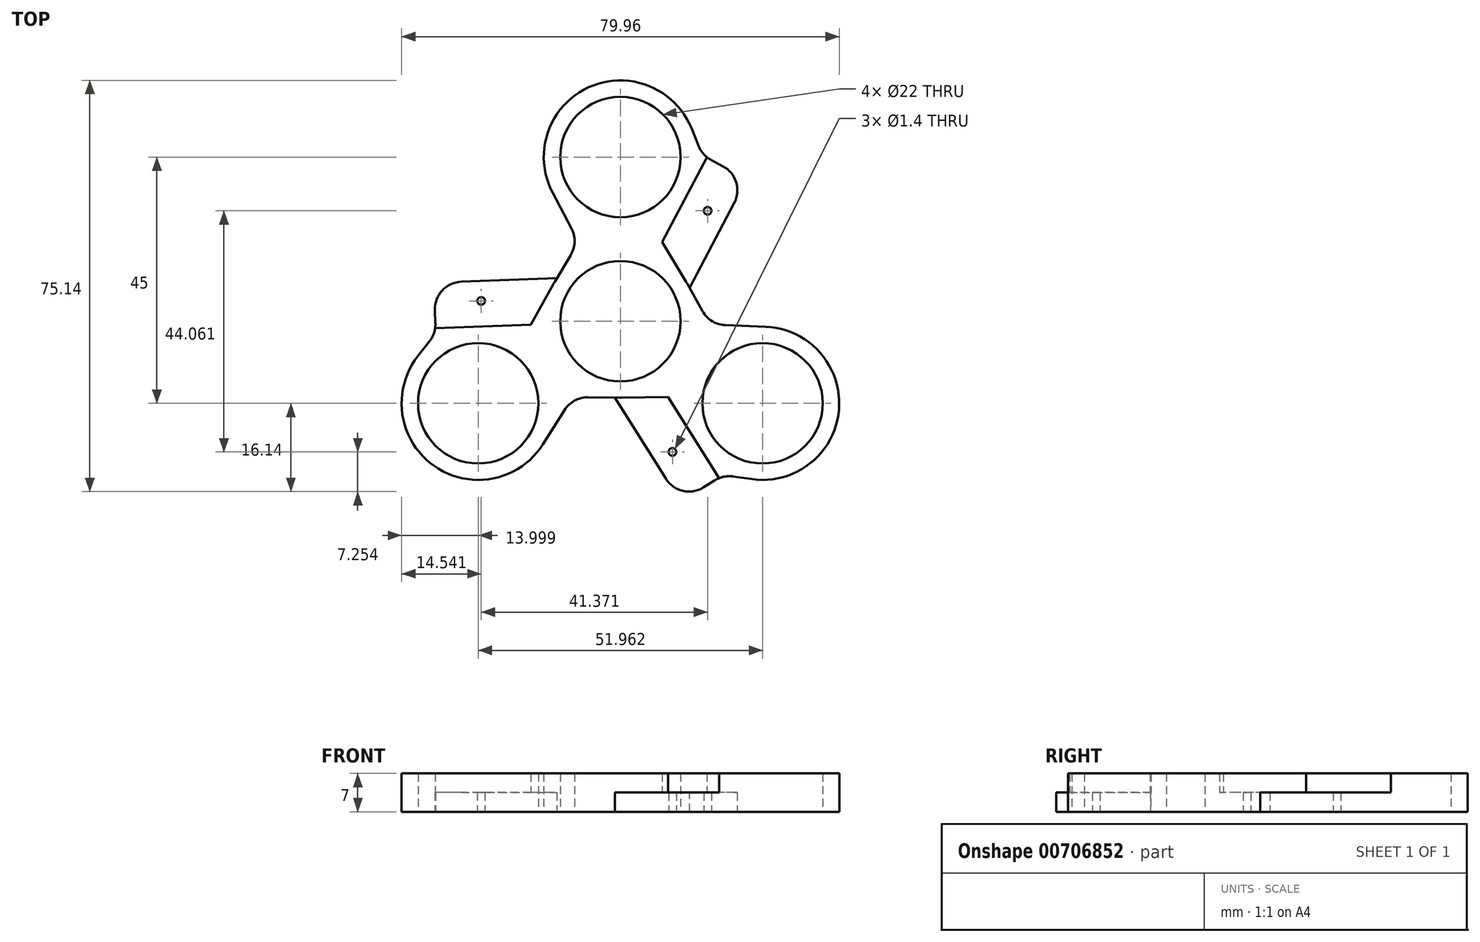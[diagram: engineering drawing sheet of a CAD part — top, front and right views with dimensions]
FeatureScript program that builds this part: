
annotation { "Feature Type Name" : "Feature", "Feature Type Description" : "" }
export const myFeature = defineFeature(function(context is Context, id is Id, definition is map)
    precondition{}
    {
        {
            var Q0;
            Q0=qCreatedBy(makeId("Top.planeOp"),FACE);
            var sketch = newSketch(context, id + "F0", { "sketchPlane" : qUnion([Q0])});
            skCircle(sketch, "E0", {"center": v(0, 0) * mm, "radius": 11 * mm});
            skLineSegment(sketch, "E1", {"start": v(0, 0) * mm, "end": v(0, 30) * mm});
            skCircle(sketch, "E2", {"center": v(0, 30) * mm, "radius": 11 * mm});
            skCircle(sketch, "E3", {"center": v(0, 30) * mm, "radius": 14 * mm});
            skCircle(sketch, "E4", {"center": v(0, 0) * mm, "radius": 14 * mm});
            skLineSegment(sketch, "E5", {"start": v(0, 0) * mm, "end": v(12.38, 23.47) * mm});
            skLineSegment(sketch, "E6", {"start": v(12, 7.2) * mm, "end": v(7.64, 14.48) * mm});
            skLineSegment(sketch, "E7", {"start": v(18.7, 28.34) * mm, "end": v(16.58, 29.46) * mm});
            skLineSegment(sketch, "E8", {"start": v(20.8, 21.59) * mm, "end": v(12.6, 6.08) * mm});
            skLineSegment(sketch, "E9.MirrorCS", {"start": v(-12, 7.2) * mm, "end": v(-9.09, 12.06) * mm});
            skPoint(sketch, "E10", {"position": v(19.18, 18.53) * mm});
            skPoint(sketch, "E11.visualSharp", {"position": v(23.12, 26.01) * mm});
            skArc(sketch, "E11.filletArc", {"start": v(20.8, 21.59) * mm, "mid": v(21.14, 25.4) * mm, "end": v(18.7, 28.34) * mm});
            skLineSegment(sketch, "E12", {"start": v(14.27, 32.02) * mm, "end": v(13, 35.21) * mm});
            skArc(sketch, "E13.filletArc", {"start": v(14.27, 32.02) * mm, "mid": v(15.2, 30.54) * mm, "end": v(16.58, 29.46) * mm});
            skPoint(sketch, "E14", {"position": v(15.81, 29.96) * mm});
            skLineSegment(sketch, "E15", {"start": v(12.38, 23.47) * mm, "end": v(15.81, 29.96) * mm});
            skLineSegment(sketch, "E16", {"start": v(-8.95, 16.97) * mm, "end": v(-12.38, 23.47) * mm});
            skPoint(sketch, "E17.visualSharp", {"position": v(-7.64, 14.48) * mm});
            skArc(sketch, "E17.filletArc", {"start": v(-9.09, 12.06) * mm, "mid": v(-8.38, 14.5) * mm, "end": v(-8.95, 16.97) * mm});
            skPoint(sketch, "E18", {"position": v(15.93, 20.18) * mm});
            skCircle(sketch, "E19", {"center": v(15.93, 20.18) * mm, "radius": 0.7 * mm});
            skLineSegment(sketch, "E20", {"start": v(15.81, 29.96) * mm, "end": v(7.64, 14.48) * mm});
            skSolve(sketch);
        }
        {
            var Q0;
            Q0=makeQuery(id+"F0.imprint","IMPRINT",FACE,{"disambiguationData":[TD([[makeQuery(id+"F0.imprint","IMPRINT",EDGE,{"derivedFrom":sQuery(id+"F0.wireOp",EDGE,"E2")}),-1.0]])]});
            var Q1;
            {var subQ4=sQuery(id+"F0.wireOp",EDGE,"E1");var subQ5=sQuery(id+"F0.wireOp",EDGE,"E0");var subQ6=makeQuery(id+"F0.imprint","INTERSECT",VERTEX,{"derivedFrom":[subQ5,subQ4]});Q1=makeQuery(id+"F0.imprint","IMPRINT",FACE,{"disambiguationData":[TD([[makeQuery(id+"F0.imprint","IMPRINT",EDGE,{"disambiguationData":[TD([[subQ6,-1.0]])],"derivedFrom":subQ5}),-1.0]])]});}
            var Q2;
            {var subQ0=sQuery(id+"F0.wireOp",EDGE,"E1");var subQ1=sQuery(id+"F0.wireOp",EDGE,"E0");var subQ2=makeQuery(id+"F0.imprint","INTERSECT",VERTEX,{"derivedFrom":[subQ1,subQ0]});Q2=makeQuery(id+"F0.imprint","IMPRINT",FACE,{"disambiguationData":[TD([[makeQuery(id+"F0.imprint","IMPRINT",EDGE,{"disambiguationData":[TD([[subQ2,1.0]])],"derivedFrom":subQ1}),-1.0]])]});}
            var Q3;
            {var subQ4=sQuery(id+"F0.wireOp",EDGE,"E1");var subQ6=sQuery(id+"F0.wireOp",EDGE,"E3");var subQ8=makeQuery(id+"F0.imprint","INTERSECT",VERTEX,{"derivedFrom":[subQ4,subQ6]});Q3=makeQuery(id+"F0.imprint","IMPRINT",FACE,{"disambiguationData":[TD([[makeQuery(id+"F0.imprint","IMPRINT",EDGE,{"disambiguationData":[TD([[subQ8,1.0]])],"derivedFrom":subQ4}),-1.0]])]});}
            var Q4;
            {var subQ0=sQuery(id+"F0.wireOp",EDGE,"E9.MirrorCS");Q4=makeQuery(id+"F0.imprint","IMPRINT",FACE,{"disambiguationData":[TD([[makeQuery(id+"F0.imprint","IMPRINT",EDGE,{"derivedFrom":subQ0}),-1.0]])]});}
            var Q5;
            {var subQ0=sQuery(id+"F0.wireOp",EDGE,"E12");Q5=makeQuery(id+"F0.imprint","IMPRINT",FACE,{"disambiguationData":[TD([[makeQuery(id+"F0.imprint","IMPRINT",EDGE,{"derivedFrom":subQ0}),1.0]])]});}
            var Q6;
            {var subQ0=sQuery(id+"F0.wireOp",EDGE,"E6");Q6=makeQuery(id+"F0.imprint","IMPRINT",FACE,{"disambiguationData":[TD([[makeQuery(id+"F0.imprint","IMPRINT",EDGE,{"derivedFrom":subQ0}),1.0]])]});}
            extrude(context, id + "F1", {"entities" : qUnion([Q0, Q1, Q2, Q3, Q4, Q5, Q6]), "depth" : 7 * mm, "offsetDistance" : 25 * mm});
        }
        {
            var Q0;
            {var subQ2=sQuery(id+"F0.wireOp",EDGE,"E6");Q0=makeQuery(id+"F0.imprint","IMPRINT",FACE,{"disambiguationData":[TD([[makeQuery(id+"F0.imprint","IMPRINT",EDGE,{"derivedFrom":subQ2}),-1.0]])]});}
            extrude(context, id + "F2", {"entities" : qUnion([Q0]), "operationType" : NewBodyOperationType.ADD, "depth" : 3.5 * mm, "offsetDistance" : 25 * mm});
        }
        {
            var Q0;
            Q0=qCreatedBy(makeId("Right.planeOp"),FACE);
            var sketch = newSketch(context, id + "F3", { "sketchPlane" : qUnion([Q0])});
            skLineSegment(sketch, "E21", {"start": v(0, 0) * mm, "end": v(0, 20) * mm, "construction": true});
            skSolve(sketch);
        }
        {
            var Q0;
            Q0=makeQuery(id+"F1.opExtrude","SWEPT_BODY",BODY,{"disambiguationData":[OSD([sQuery(id+"F0.wireOp",EDGE,"E0"),sQuery(id+"F0.wireOp",EDGE,"E2"),sQuery(id+"F0.wireOp",EDGE,"E3"),sQuery(id+"F0.wireOp",EDGE,"E4"),sQuery(id+"F0.wireOp",EDGE,"E6"),sQuery(id+"F0.wireOp",EDGE,"E9.MirrorCS"),sQuery(id+"F0.wireOp",EDGE,"E12"),sQuery(id+"F0.wireOp",EDGE,"E13.filletArc"),sQuery(id+"F0.wireOp",EDGE,"E16"),sQuery(id+"F0.wireOp",EDGE,"E17.filletArc"),sQuery(id+"F0.wireOp",EDGE,"E20")])]});
            var Q1;
            Q1=sQuery(id+"F3.wireOp",EDGE,"E21");
            circularPattern(context, id + "F4", {"operationType" : NewBodyOperationType.ADD, "entities" : qUnion([Q0]), "axis" : qUnion([Q1]), "angle" : 360 * degree, "instanceCount" : 3, "equalSpace" : true});
        }
    });
